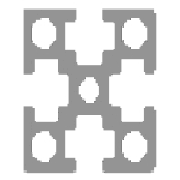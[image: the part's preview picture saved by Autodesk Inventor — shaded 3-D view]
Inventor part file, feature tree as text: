
AUTODESK INVENTOR PART (.ipt)
format: ipt  version: 2018.2 (Build 222227000, 227)  size: 343,040 bytes
history: native  units: mm
features: other x5, sketch x4, extrude x3, projected_geometry x1
ambient origin geometry x8: Origin, YZ Plane, XZ Plane, XY Plane, X Axis, Y Axis, Z Axis, Center Point
bodies: Body1 (feature_tree)
feature tree (13):
  other  "被駆動長さ"
  other  "フレーム ジェネレータ"
  other  "開始平面"
  other  "終了平面"
  extrude  "ボディ"  Depth=4.0mm
  extrude  "押し出し7"  Depth=3.7mm
  extrude  "押し出し8"  Depth=0.5mm
  sketch  "スケッチ4"
  other  "作業平面4"
  sketch  "スケッチ5"
  sketch  "スケッチ9"
  projected_geometry  "投影ループ4"
  sketch  "スケッチ10"
